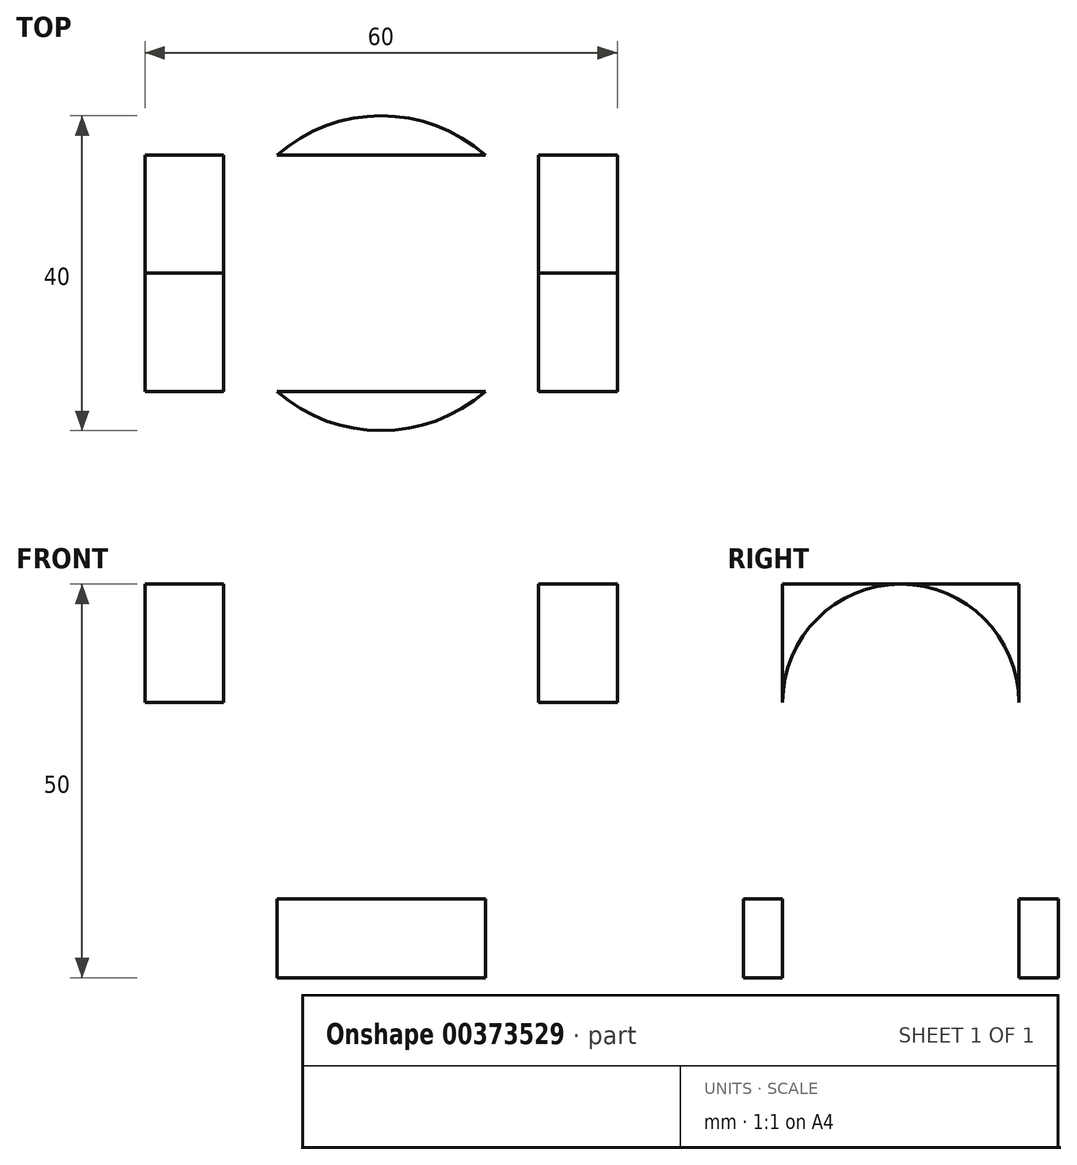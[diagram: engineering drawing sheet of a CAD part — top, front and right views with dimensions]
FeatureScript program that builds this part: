
annotation { "Feature Type Name" : "Feature", "Feature Type Description" : "" }
export const myFeature = defineFeature(function(context is Context, id is Id, definition is map)
    precondition{}
    {
        {
            var Q0;
            Q0=qCreatedBy(makeId("Top.planeOp"),FACE);
            var sketch = newSketch(context, id + "F0", { "sketchPlane" : qUnion([Q0])});
            skLineSegment(sketch, "E0", {"start": v(0, 0) * mm, "end": v(60, 0) * mm});
            skLineSegment(sketch, "E1", {"start": v(60, 0) * mm, "end": v(60, 30) * mm});
            skLineSegment(sketch, "E2", {"start": v(60, 30) * mm, "end": v(0, 30) * mm});
            skLineSegment(sketch, "E3", {"start": v(0, 30) * mm, "end": v(0, 0) * mm});
            skCircle(sketch, "E4", {"center": v(30, 15) * mm, "radius": 10 * mm});
            skCircle(sketch, "E5", {"center": v(30, 15) * mm, "radius": 20 * mm});
            skLineSegment(sketch, "E6", {"start": v(10, 30) * mm, "end": v(10, 0) * mm});
            skLineSegment(sketch, "E7", {"start": v(50, 30) * mm, "end": v(50, 0) * mm});
            skSolve(sketch);
        }
        {
            var Q0;
            Q0 = qSketchRegion(id + "F0", true);
            extrude(context, id + "F1", {"entities" : qUnion([Q0]), "depth" : 10 * mm});
        }
        {
            var Q0;
            {var subQ4=sQuery(id+"F0.wireOp",EDGE,"E3");Q0=makeQuery(id+"F0.imprint","IMPRINT",FACE,{"disambiguationData":[TD([[makeQuery(id+"F0.imprint","IMPRINT",EDGE,{"derivedFrom":subQ4}),1.0]])]});}
            var Q1;
            {var subQ4=sQuery(id+"F0.wireOp",EDGE,"E1");Q1=makeQuery(id+"F0.imprint","IMPRINT",FACE,{"disambiguationData":[TD([[makeQuery(id+"F0.imprint","IMPRINT",EDGE,{"derivedFrom":subQ4}),1.0]])]});}
            extrude(context, id + "F2", {"entities" : qUnion([Q0, Q1]), "operationType" : NewBodyOperationType.ADD, "depth" : 50 * mm});
        }
        {
            var Q0;
            {var subQ0=sQuery(id+"F0.wireOp",EDGE,"E3");Q0=makeQuery(id+"F2.boolean.opBoolean","MERGE",FACE,{"derivedFrom":[makeQuery(id+"F1.opExtrude","SWEPT_FACE",FACE,{"disambiguationData":[OSD([subQ0])]}),makeQuery(id+"F2.opExtrude","SWEPT_FACE",FACE,{"disambiguationData":[OSD([subQ0])]})]});}
            var sketch = newSketch(context, id + "F3", { "sketchPlane" : qUnion([Q0])});
            skArc(sketch, "E8", {"start": v(-30, 35) * mm, "mid": v(-15, 50) * mm, "end": v(0, 35) * mm});
            skPoint(sketch, "E8.centerSnap0", {"position": v(-15, 50) * mm});
            skCircle(sketch, "E9", {"center": v(-15, 35) * mm, "radius": 7.5 * mm});
            skSolve(sketch);
        }
        {
            var Q0;
            Q0 = qSketchRegion(id + "F3", true);
            var Q1;
            {var subQ0=sQuery(id+"F3.wireOp",EDGE,"E8");var subQ1=sQuery(id+"F0.wireOp",EDGE,"E3");var subQ5=makeQuery(id+"F2.opExtrude","CAP_EDGE",EDGE,{"disambiguationData":[OSD([subQ1])],"isStart":false});var subQ6=makeQuery(id+"F3.imprint","INTERSECT",VERTEX,{"derivedFrom":[subQ5,subQ0]});Q1=makeQuery(id+"F3.imprint","IMPRINT",FACE,{"disambiguationData":[TD([[makeQuery(id+"F3.imprint","IMPRINT",EDGE,{"disambiguationData":[TD([[subQ6,1.0]])],"derivedFrom":subQ0}),1.0]])]});}
            var Q2;
            {var subQ0=sQuery(id+"F3.wireOp",EDGE,"E8");var subQ1=sQuery(id+"F0.wireOp",EDGE,"E3");var subQ5=makeQuery(id+"F2.opExtrude","CAP_EDGE",EDGE,{"disambiguationData":[OSD([subQ1])],"isStart":false});var subQ6=makeQuery(id+"F3.imprint","INTERSECT",VERTEX,{"derivedFrom":[subQ5,subQ0]});Q2=makeQuery(id+"F3.imprint","IMPRINT",FACE,{"disambiguationData":[TD([[makeQuery(id+"F3.imprint","IMPRINT",EDGE,{"disambiguationData":[TD([[subQ6,-1.0]])],"derivedFrom":subQ0}),1.0]])]});}
            extrude(context, id + "F4", {"entities" : qUnion([Q0, Q1, Q2]), "operationType" : NewBodyOperationType.REMOVE, "endBound" : BoundingType.THROUGH_ALL, "oppositeDirection" : true, "depth" : 25 * mm});
        }
    });
